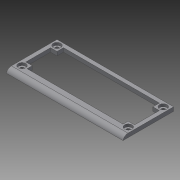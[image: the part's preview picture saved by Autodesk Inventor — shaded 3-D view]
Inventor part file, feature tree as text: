
AUTODESK INVENTOR PART (.ipt)
format: ipt  version: 2015 (Build 190159000, 159)  size: 187,904 bytes
history: native  units: mm
features: extrude x10, sketch x10, other x1, fillet x1
ambient origin geometry x8: Origin, YZ Plane, XZ Plane, XY Plane, X Axis, Y Axis, Z Axis, Center Point
bodies: Body1 (feature_tree), Body2 (feature_tree)
feature tree (22):
  other  "ソリッド1"
  extrude  "押し出し1"  Depth=90.0mm
  extrude  "押し出し2"  Depth=7.0mm
  extrude  "押し出し3"  Depth=3.0mm TaperAngle=0.0deg
  extrude  "押し出し4"  Depth=5.8mm
  fillet  "フィレット1"  Radius=5.8mm
  extrude  "押し出し5"  Depth=3.9mm
  extrude  "押し出し6"  Depth=3.9mm
  extrude  "押し出し7"  Depth=82.0mm
  extrude  "押し出し8"  Depth=4.0mm
  extrude  "押し出し9"  Depth=2.0mm TaperAngle=0.0deg
  extrude  "押し出し10"  Depth=3.0mm
  sketch  "スケッチ1"
  sketch  "スケッチ2"
  sketch  "スケッチ3"
  sketch  "スケッチ4"
  sketch  "スケッチ6"
  sketch  "スケッチ7"
  sketch  "スケッチ8"
  sketch  "スケッチ9"
  sketch  "スケッチ10"
  sketch  "スケッチ11"
